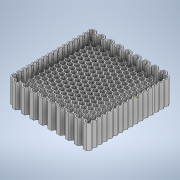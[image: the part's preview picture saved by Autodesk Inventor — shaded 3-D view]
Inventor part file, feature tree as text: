
AUTODESK INVENTOR PART (.ipt)
format: ipt  version: 2021 (Build 250183000, 183)  size: 4,401,152 bytes
history: native  units: mm
features: sketch x12, extrude x10, pattern_linear x5, other x2, fillet x2, plane x1
ambient origin geometry x8: Origin, YZ Plane, XZ Plane, XY Plane, X Axis, Y Axis, Z Axis, Center Point
bodies: Solid1 (feature_tree)
feature tree (32):
  extrude  "Extrusion1"  Depth=65.11mm
  extrude  "Extrusion2"  Depth=32.555mm
  pattern_linear  "Rectangular Pattern1"  Count1=8 Spacing1=8.3mm
  extrude  "Extrusion3"  Depth=4.3641mm
  pattern_linear  "Rectangular Pattern2"  Spacing1=0.9mm  [1 undecoded]
  pattern_linear  "Rectangular Pattern3"  Spacing1=0.9mm  [1 undecoded]
  other  "Work Point1"
  extrude  "Extrusion4"  Depth=0.9mm
  extrude  "Extrusion5"  Depth=2.0mm
  extrude  "Extrusion6"  Depth=0.3mm
  fillet  "Fillet2"  Radius=0.45mm
  pattern_linear  "Rectangular Pattern4"  Spacing1=0.45mm  [1 undecoded]
  extrude  "Extrusion7"  Depth=0.3mm
  extrude  "Extrusion8"  Depth=0.9mm
  fillet  "Fillet4"  Radius=7.558mm
  pattern_linear  "Rectangular Pattern5"  Spacing1=65.12mm  [1 undecoded]
  extrude  "Extrusion9"  Depth=65.12mm
  plane  "Work Plane2"
  extrude  "Extrusion10"  Depth=0.3mm
  sketch  "Sketch1"  dims[d0=65.11mm d1=65.11mm]
  sketch  "Sketch2"  dims[d2=32.555mm d3=32.555mm]
  sketch  "Sketch3"  dims[d4=1.5mm d5=0.0mm]
  other  "Diffuser"
  sketch  "Sketch5"  dims[d6=4.9mm]
  sketch  "Sketch6"  dims[d7=4.9mm]
  sketch  "Sketch7"  dims[d8=1.05mm]
  sketch  "Sketch8"  dims[d9=1.2mm]
  sketch  "Sketch9"  dims[d10=1.6mm d11=0.0mm d12=80.0mm d14=8.3mm d15=80.0mm d17=8.26mm]
  sketch  "Sketch10"  dims[d23=20.0mm d24=0.0mm d25=160.0mm d27=4.3641mm]
  sketch  "Sketch11"  dims[d29=0.9mm]
  sketch  "Sketch12"  dims[d49=2.0mm]
  sketch  "Sketch14"  dims[d57=0.9mm d63=0.9mm d64=0.9mm d65=0.9mm d67=2.0mm d70=0.45mm d71=0.45mm d72=0.45mm d73=0.45mm d74=0.9mm d75=90.0mm d77=7.558mm d78=65.12mm d79=65.12mm d80=2.6mm d81=2.601884mm d82=3.894mm d83=3.893652mm d84=5.0mm d85=0.0mm d86=1.5mm d87=0.5mm d88=0.0mm d90=0.3mm d102=0.0mm d103=0.0mm d105=0.1mm d107=0.15mm d108=0.3mm d109=150.0mm d111=4.3641mm d112=1.5mm d113=0.5mm d114=0.0mm d115=0.3mm d116=0.15mm d117=1.5mm d118=0.0mm d119=0.1mm d120=150.0mm d122=4.3641mm d123=0.5mm d124=0.5mm d125=0.5mm d126=0.5mm d127=2.0mm d128=0.0mm d130=-4.0mm d131=0.8mm d132=0.5mm d134=0.8mm d135=0.5mm d136=0.3mm d137=0.0mm]
note: 4 required parameter values undecoded (feature->parameter linkage not recoverable at this tier; creation-order binding heuristic only, values carry confidence <= 0.55)
